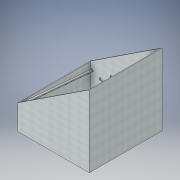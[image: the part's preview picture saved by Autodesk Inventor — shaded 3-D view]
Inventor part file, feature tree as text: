
AUTODESK INVENTOR PART (.ipt)
format: ipt  version: 2019.4 (Build 234330000, 330)  size: 299,520 bytes
history: native  units: mm
features: extrude x7, sketch x7, other x2, mirror x1
ambient origin geometry x8: Origin, YZ Plane, XZ Plane, XY Plane, X Axis, Y Axis, Z Axis, Center Point
bodies: Body1 (feature_tree)
feature tree (17):
  other  "Sólido1"
  extrude  "Extrusão1"  Depth=10.0mm TaperAngle=0.0deg
  extrude  "Extrusão2"  Depth=1000.0mm
  extrude  "Extrusão3"  Depth=350.0mm
  extrude  "Extrusão4"  Depth=10.0mm
  extrude  "Extrusão5"  Depth=10.0mm
  extrude  "Extrusão6"  Depth=6.0mm
  extrude  "Extrusão7"  Depth=10.0mm TaperAngle=0.0deg
  other  "Plano de trabalho1"
  mirror  "Espelhamento1"
  sketch  "Esboço1"  dims[d0=1000.0mm d1=0.0mm d2=10.0mm d3=0.0mm]
  sketch  "Esboço2"  dims[d4=10.0mm d5=0.0mm d6=1000.0mm]
  sketch  "Esboço3"  dims[d7=1000.0mm d8=350.0mm]
  sketch  "Esboço4"  dims[d10=10.0mm d11=14.835299mm]
  sketch  "Esboço5"  dims[d13=20.0mm d14=10.0mm]
  sketch  "Esboço6"  dims[d15=30.0mm d16=0.0mm d18=6.0mm]
  sketch  "Esboço7"  dims[d19=10.0mm d20=0.0mm d21=10.0mm d22=0.0mm d23=202.0mm d24=10.0mm d25=10.0mm d26=10.0mm d27=30.0mm d28=60.0mm d35=202.0mm d36=10.0mm d37=10.0mm d38=10.0mm d39=30.0mm d40=60.0mm d41=202.0mm d42=10.0mm d43=10.0mm d44=10.0mm d45=30.0mm d46=60.0mm d47=202.0mm d48=10.0mm d49=10.0mm d50=10.0mm d51=30.0mm d52=60.0mm d53=100.0mm d54=202.0mm d55=10.0mm d56=10.0mm d57=10.0mm d58=30.0mm d59=60.0mm d60=90.0mm d61=90.0mm d62=90.0mm d63=90.0mm d64=764.308998mm d65=140.0mm d66=10.0mm d67=0.0mm]
